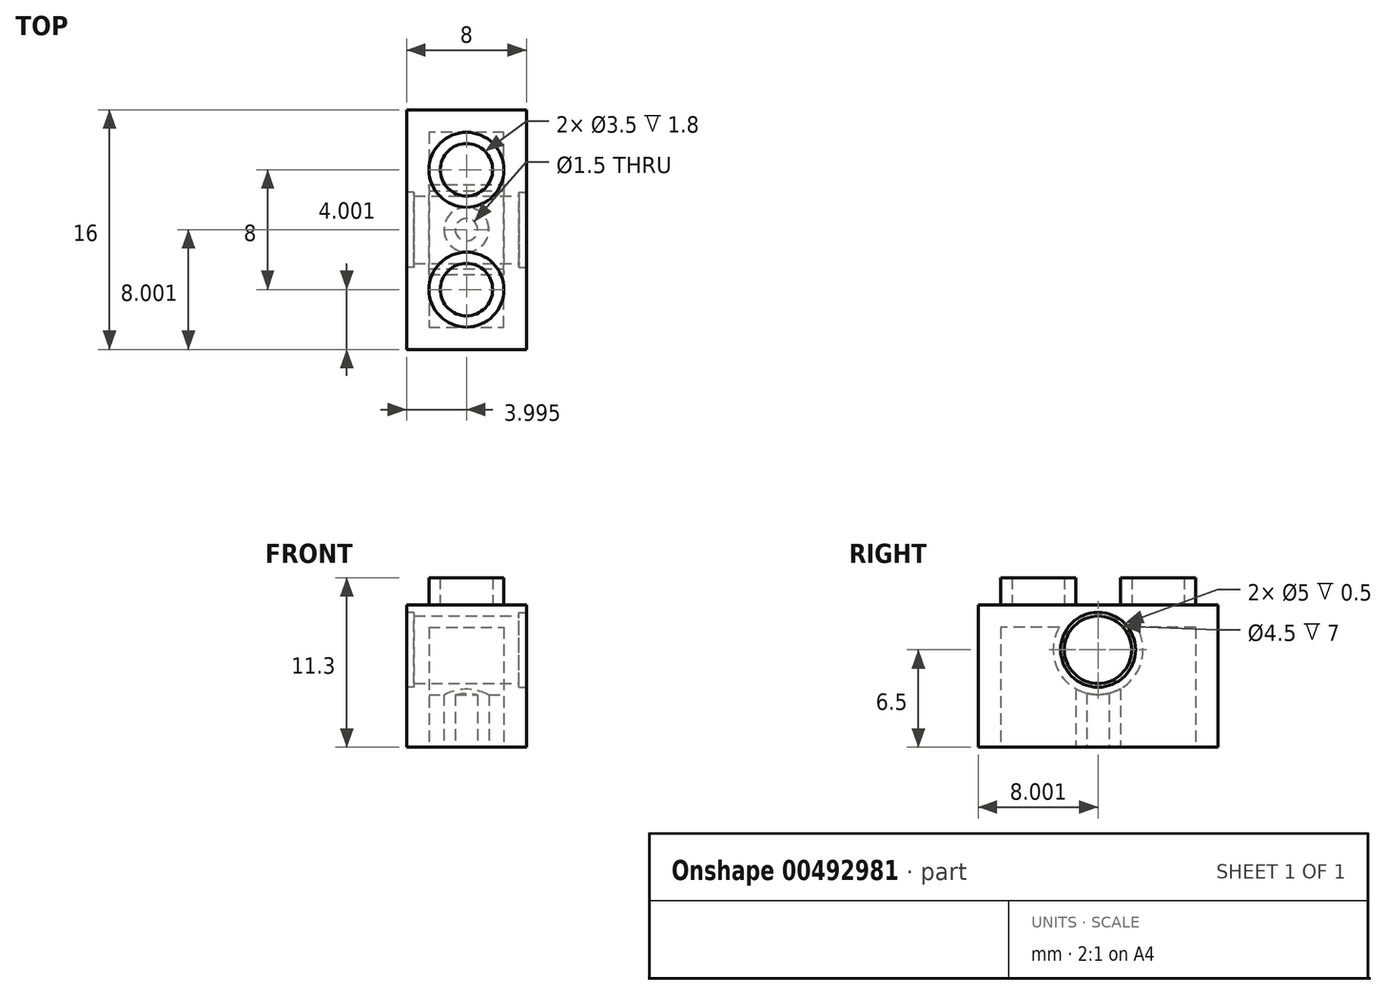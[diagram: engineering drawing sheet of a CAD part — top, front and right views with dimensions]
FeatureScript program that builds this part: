
annotation { "Feature Type Name" : "Feature", "Feature Type Description" : "" }
export const myFeature = defineFeature(function(context is Context, id is Id, definition is map)
    precondition{}
    {
        {
            var Q0;
            Q0=qCreatedBy(makeId("Top.planeOp"),FACE);
            var sketch = newSketch(context, id + "F0", { "sketchPlane" : qUnion([Q0])});
            skLineSegment(sketch, "E0.bottom", {"start": v(-35.9, 8.93) * mm, "end": v(-27.9, 8.93) * mm});
            skLineSegment(sketch, "E0.top", {"start": v(-35.9, -7.07) * mm, "end": v(-27.9, -7.07) * mm});
            skLineSegment(sketch, "E0.left", {"start": v(-35.9, 8.93) * mm, "end": v(-35.9, -7.07) * mm});
            skLineSegment(sketch, "E0.right", {"start": v(-27.9, 8.93) * mm, "end": v(-27.9, -7.07) * mm});
            skSolve(sketch);
        }
        {
            var Q0;
            Q0=makeQuery(id+"F0.imprint","IMPRINT",FACE,{"disambiguationData":[TD([[makeQuery(id+"F0.imprint","IMPRINT",EDGE,{"derivedFrom":sQuery(id+"F0.wireOp",EDGE,"E0.bottom")}),-1.0]])]});
            var sketch = newSketch(context, id + "F1", { "sketchPlane" : qUnion([Q0])});
            skLineSegment(sketch, "E1.0", {"start": v(-34.4, 7.43) * mm, "end": v(-34.4, -5.57) * mm});
            skLineSegment(sketch, "E1.1", {"start": v(-29.4, 7.43) * mm, "end": v(-34.4, 7.43) * mm});
            skLineSegment(sketch, "E1.2", {"start": v(-29.4, -5.57) * mm, "end": v(-29.4, 7.43) * mm});
            skLineSegment(sketch, "E1.3", {"start": v(-34.4, -5.57) * mm, "end": v(-29.4, -5.57) * mm});
            skSolve(sketch);
        }
        {
            var Q0;
            Q0=makeQuery(id+"F1.imprint","IMPRINT",FACE,{"disambiguationData":[TD([[makeQuery(id+"F1.imprint","IMPRINT",EDGE,{"derivedFrom":sQuery(id+"F1.wireOp",EDGE,"E1.0")}),-1.0]])]});
            extrude(context, id + "F2", {"entities" : qUnion([Q0]), "depth" : 8 * mm});
        }
        {
            var Q0;
            Q0=makeQuery(id+"F2.opExtrude","CAP_FACE",FACE,{"disambiguationData":[OSD([sQuery(id+"F0.wireOp",EDGE,"E0.bottom"),sQuery(id+"F0.wireOp",EDGE,"E0.top"),sQuery(id+"F0.wireOp",EDGE,"E0.left"),sQuery(id+"F0.wireOp",EDGE,"E0.right"),sQuery(id+"F1.wireOp",EDGE,"E1.0"),sQuery(id+"F1.wireOp",EDGE,"E1.1"),sQuery(id+"F1.wireOp",EDGE,"E1.2"),sQuery(id+"F1.wireOp",EDGE,"E1.3")])],"isStart":false});
            var sketch = newSketch(context, id + "F3", { "sketchPlane" : qUnion([Q0])});
            skLineSegment(sketch, "E2.bottom", {"start": v(-35.9, -7.07) * mm, "end": v(-27.9, -7.07) * mm});
            skLineSegment(sketch, "E2.top", {"start": v(-35.9, 8.93) * mm, "end": v(-27.9, 8.93) * mm});
            skLineSegment(sketch, "E2.left", {"start": v(-35.9, -7.07) * mm, "end": v(-35.9, 8.93) * mm});
            skLineSegment(sketch, "E2.right", {"start": v(-27.9, -7.07) * mm, "end": v(-27.9, 8.93) * mm});
            skSolve(sketch);
        }
        {
            var Q0;
            Q0=makeQuery(id+"F3.imprint","IMPRINT",FACE,{"disambiguationData":[TD([[makeQuery(id+"F3.imprint","IMPRINT",EDGE,{"derivedFrom":sQuery(id+"F3.wireOp",EDGE,"E2.bottom")}),1.0]])]});
            var Q1;
            Q1=makeQuery(id+"F3.imprint","IMPRINT",FACE,{"disambiguationData":[TD([[makeQuery(id+"F3.imprint","IMPRINT",EDGE,{"derivedFrom":makeQuery(id+"F2.opExtrude","CAP_EDGE",EDGE,{"disambiguationData":[OSD([sQuery(id+"F1.wireOp",EDGE,"E1.0")])],"isStart":false})}),1.0]])]});
            extrude(context, id + "F4", {"entities" : qUnion([Q0, Q1]), "operationType" : NewBodyOperationType.ADD, "depth" : 1.5 * mm});
        }
        {
            var Q0;
            Q0=makeQuery(id+"F4.opExtrude","CAP_FACE",FACE,{"disambiguationData":[OSD([sQuery(id+"F3.wireOp",EDGE,"E2.bottom"),sQuery(id+"F3.wireOp",EDGE,"E2.top"),sQuery(id+"F3.wireOp",EDGE,"E2.left"),sQuery(id+"F3.wireOp",EDGE,"E2.right")])],"isStart":false});
            var sketch = newSketch(context, id + "F5", { "sketchPlane" : qUnion([Q0])});
            skCircle(sketch, "E3", {"center": v(-31.9, -3.07) * mm, "radius": 2.5 * mm});
            skCircle(sketch, "E4", {"center": v(-31.9, 4.93) * mm, "radius": 2.5 * mm});
            skCircle(sketch, "E5.0", {"center": v(-31.9, -3.07) * mm, "radius": 1.75 * mm});
            skCircle(sketch, "E6.0", {"center": v(-31.9, 4.93) * mm, "radius": 1.75 * mm});
            skSolve(sketch);
        }
        {
            var Q0;
            Q0=makeQuery(id+"F5.imprint","IMPRINT",FACE,{"disambiguationData":[TD([[makeQuery(id+"F5.imprint","IMPRINT",EDGE,{"derivedFrom":sQuery(id+"F5.wireOp",EDGE,"E3")}),1.0]])]});
            var Q1;
            Q1=makeQuery(id+"F5.imprint","IMPRINT",FACE,{"disambiguationData":[TD([[makeQuery(id+"F5.imprint","IMPRINT",EDGE,{"derivedFrom":sQuery(id+"F5.wireOp",EDGE,"E4")}),1.0]])]});
            extrude(context, id + "F6", {"entities" : qUnion([Q0, Q1]), "operationType" : NewBodyOperationType.ADD, "depth" : 1.8 * mm});
        }
        {
            var Q0;
            Q0=makeQuery(id+"F4.boolean.opBoolean","MERGE",FACE,{"derivedFrom":[makeQuery(id+"F2.opExtrude","SWEPT_FACE",FACE,{"disambiguationData":[OSD([sQuery(id+"F0.wireOp",EDGE,"E0.right")])]}),makeQuery(id+"F4.opExtrude","SWEPT_FACE",FACE,{"disambiguationData":[OSD([sQuery(id+"F3.wireOp",EDGE,"E2.right")])]})]});
            var sketch = newSketch(context, id + "F7", { "sketchPlane" : qUnion([Q0])});
            skLineSegment(sketch, "E7", {"start": v(0.93, 9.5) * mm, "end": v(0.93, 6.5) * mm});
            skPoint(sketch, "E7.endSnap0", {"position": v(0.93, 9.5) * mm});
            skCircle(sketch, "E8", {"center": v(0.93, 6.5) * mm, "radius": 3 * mm});
            skSolve(sketch);
        }
        {
            var Q0;
            Q0=makeQuery(id+"F7.imprint","IMPRINT",FACE,{"disambiguationData":[TD([[makeQuery(id+"F7.imprint","IMPRINT",EDGE,{"derivedFrom":sQuery(id+"F7.wireOp",EDGE,"E8")}),1.0]])]});
            extrude(context, id + "F8", {"entities" : qUnion([Q0]), "operationType" : NewBodyOperationType.ADD, "oppositeDirection" : true, "depth" : 7.9 * mm});
        }
        {
            var Q0;
            Q0=makeQuery(id+"F7.imprint","IMPRINT",FACE,{"disambiguationData":[TD([[makeQuery(id+"F7.imprint","IMPRINT",EDGE,{"derivedFrom":sQuery(id+"F7.wireOp",EDGE,"E8")}),1.0]])]});
            var sketch = newSketch(context, id + "F9", { "sketchPlane" : qUnion([Q0])});
            skCircle(sketch, "E9.0", {"center": v(0.93, 6.5) * mm, "radius": 2.5 * mm});
            skLineSegment(sketch, "E10.0", {"start": v(0.93, 14.5) * mm, "end": v(-12.07, 14.5) * mm});
            skLineSegment(sketch, "E10.1", {"start": v(13.93, 14.5) * mm, "end": v(0.93, 14.5) * mm});
            skLineSegment(sketch, "E10.2", {"start": v(-12.07, 14.5) * mm, "end": v(-12.07, -5) * mm});
            skLineSegment(sketch, "E10.3", {"start": v(-12.07, -5) * mm, "end": v(13.93, -5) * mm});
            skLineSegment(sketch, "E10.4", {"start": v(13.93, -5) * mm, "end": v(13.93, 14.5) * mm});
            skCircle(sketch, "E11.0", {"center": v(0.93, 6.5) * mm, "radius": 2.25 * mm});
            skSolve(sketch);
        }
        {
            var Q0;
            Q0=makeQuery(id+"F9.imprint","IMPRINT",FACE,{"disambiguationData":[TD([[makeQuery(id+"F9.imprint","IMPRINT",EDGE,{"derivedFrom":sQuery(id+"F9.wireOp",EDGE,"E11.0")}),1.0]])]});
            extrude(context, id + "F10", {"entities" : qUnion([Q0]), "operationType" : NewBodyOperationType.REMOVE, "oppositeDirection" : true, "depth" : 25 * mm});
        }
        {
            var Q0;
            Q0=makeQuery(id+"F9.imprint","IMPRINT",FACE,{"disambiguationData":[TD([[makeQuery(id+"F9.imprint","IMPRINT",EDGE,{"derivedFrom":sQuery(id+"F9.wireOp",EDGE,"E9.0")}),1.0]])]});
            extrude(context, id + "F11", {"entities" : qUnion([Q0]), "operationType" : NewBodyOperationType.REMOVE, "oppositeDirection" : true, "depth" : .5 * mm});
        }
        {
            var Q0;
            Q0=makeQuery(id+"F4.boolean.opBoolean","MERGE",FACE,{"derivedFrom":[makeQuery(id+"F2.opExtrude","SWEPT_FACE",FACE,{"disambiguationData":[OSD([sQuery(id+"F0.wireOp",EDGE,"E0.left")])]}),makeQuery(id+"F4.opExtrude","SWEPT_FACE",FACE,{"disambiguationData":[OSD([sQuery(id+"F3.wireOp",EDGE,"E2.left")])]})]});
            var sketch = newSketch(context, id + "F12", { "sketchPlane" : qUnion([Q0])});
            skCircle(sketch, "E12.0", {"center": v(-0.93, 6.5) * mm, "radius": 2.5 * mm});
            skLineSegment(sketch, "E13.0", {"start": v(-13.93, -5) * mm, "end": v(12.07, -5) * mm});
            skLineSegment(sketch, "E13.1", {"start": v(-13.93, 14.5) * mm, "end": v(-13.93, -5) * mm});
            skLineSegment(sketch, "E13.2", {"start": v(12.07, 14.5) * mm, "end": v(-13.93, 14.5) * mm});
            skLineSegment(sketch, "E13.3", {"start": v(12.07, -5) * mm, "end": v(12.07, 14.5) * mm});
            skSolve(sketch);
        }
        {
            var Q0;
            Q0=makeQuery(id+"F12.imprint","IMPRINT",FACE,{"disambiguationData":[TD([[makeQuery(id+"F12.imprint","IMPRINT",EDGE,{"derivedFrom":sQuery(id+"F12.wireOp",EDGE,"E12.0")}),1.0]])]});
            extrude(context, id + "F13", {"entities" : qUnion([Q0]), "operationType" : NewBodyOperationType.REMOVE, "oppositeDirection" : true, "depth" : .5 * mm});
        }
        {
            var Q0;
            Q0=qCreatedBy(makeId("Top.planeOp"),FACE);
            var sketch = newSketch(context, id + "F14", { "sketchPlane" : qUnion([Q0])});
            skLineSegment(sketch, "E14", {"start": v(-35.9, 0.93) * mm, "end": v(-31.9, 0.93) * mm});
            skCircle(sketch, "E15", {"center": v(-31.9, 0.93) * mm, "radius": 1.5 * mm});
            skCircle(sketch, "E16.0", {"center": v(-31.9, 0.93) * mm, "radius": 0.75 * mm});
            skSolve(sketch);
        }
        {
            var Q0;
            Q0=makeQuery(id+"F14.imprint","IMPRINT",FACE,{"disambiguationData":[TD([[makeQuery(id+"F14.imprint","IMPRINT",EDGE,{"derivedFrom":sQuery(id+"F14.wireOp",EDGE,"E15")}),1.0]])]});
            extrude(context, id + "F15", {"entities" : qUnion([Q0]), "operationType" : NewBodyOperationType.ADD, "depth" : 4.2 * mm});
        }
    });
